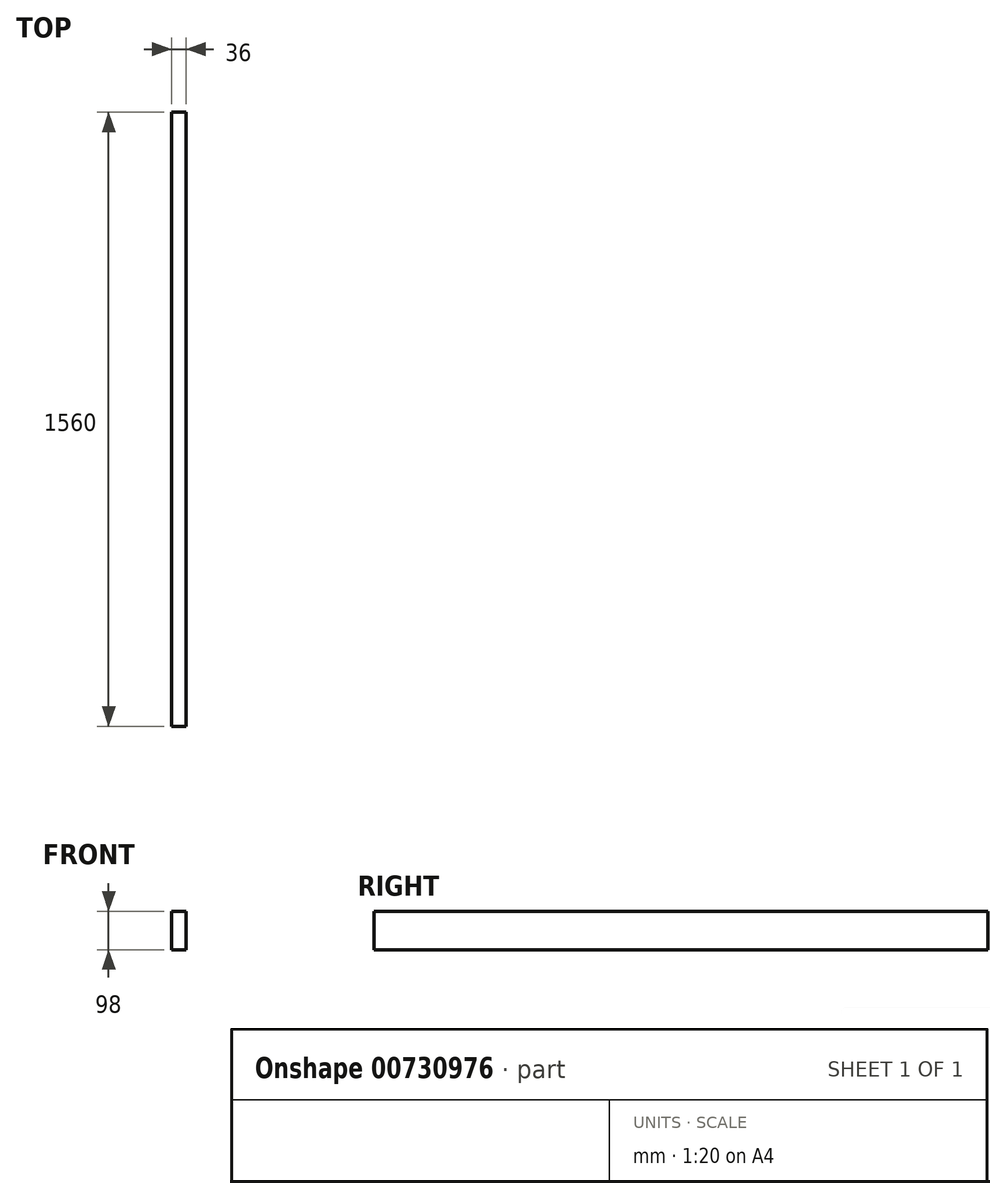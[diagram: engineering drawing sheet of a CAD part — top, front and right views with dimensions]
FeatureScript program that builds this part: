
annotation { "Feature Type Name" : "Feature", "Feature Type Description" : "" }
export const myFeature = defineFeature(function(context is Context, id is Id, definition is map)
    precondition{}
    {
        {
            var Q0;
            Q0=qCreatedBy(makeId("Front.planeOp"),FACE);
            var sketch = newSketch(context, id + "F0", { "sketchPlane" : qUnion([Q0])});
            skLineSegment(sketch, "E0.bottom", {"start": v(18, -49) * mm, "end": v(-18, -49) * mm});
            skLineSegment(sketch, "E0.top", {"start": v(18, 49) * mm, "end": v(-18, 49) * mm});
            skLineSegment(sketch, "E0.left", {"start": v(18, -49) * mm, "end": v(18, 49) * mm});
            skLineSegment(sketch, "E0.right", {"start": v(-18, -49) * mm, "end": v(-18, 49) * mm});
            skPoint(sketch, "E0.middle", {"position": v(0, 0) * mm});
            skSolve(sketch);
        }
        {
            var Q0;
            Q0 = qSketchRegion(id + "F0", true);
            extrude(context, id + "F1", {"entities" : qUnion([Q0]), "depth" : 1560 * mm, "offsetDistance" : 25 * mm});
        }
    });
